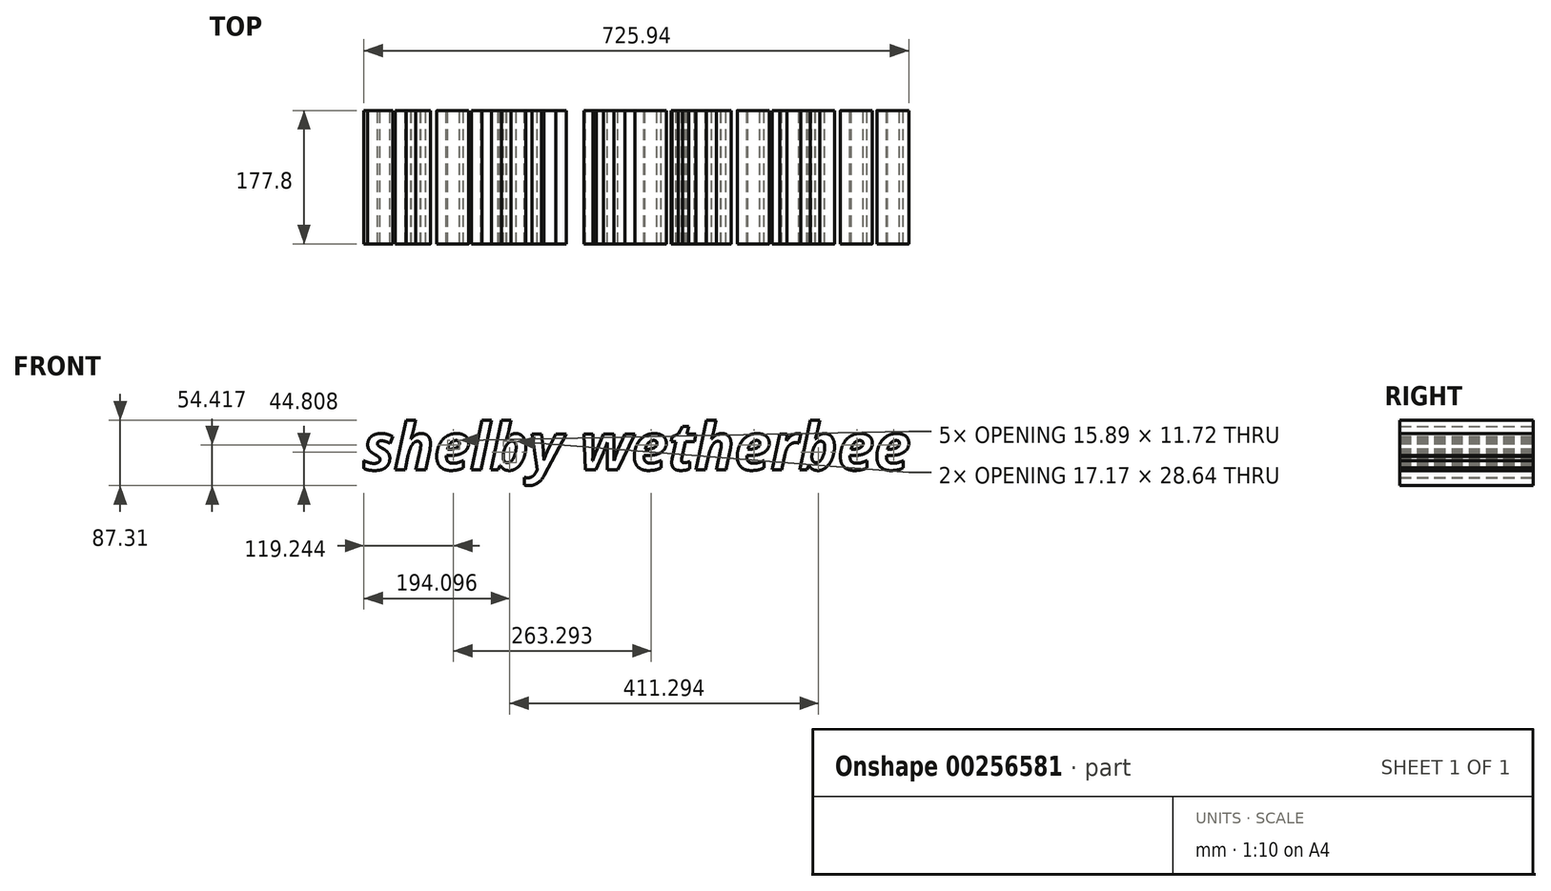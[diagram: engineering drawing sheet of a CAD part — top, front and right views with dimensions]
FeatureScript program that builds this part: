
annotation { "Feature Type Name" : "Feature", "Feature Type Description" : "" }
export const myFeature = defineFeature(function(context is Context, id is Id, definition is map)
    precondition{}
    {
        {
            var Q0;
            Q0=qCreatedBy(makeId("Front.planeOp"),FACE);
            var sketch = newSketch(context, id + "F0", { "sketchPlane" : qUnion([Q0])});
            skText(sketch, "E0", { "text": "shelby wetherbee", "fontName": "OpenSans-BoldItalic.ttf"});
            const initialGuessF0  = {"E0": [-0.30863, -0.03305, 1, 0, 0.06285]};
            skSetInitialGuess(sketch, initialGuessF0);
            skSolve(sketch);
        }
        {
            var Q0;
            Q0 = qSketchRegion(id + "F0", true);
            extrude(context, id + "F1", {"entities" : qUnion([Q0]), "depth" : 177.8 * mm});
        }
    });
